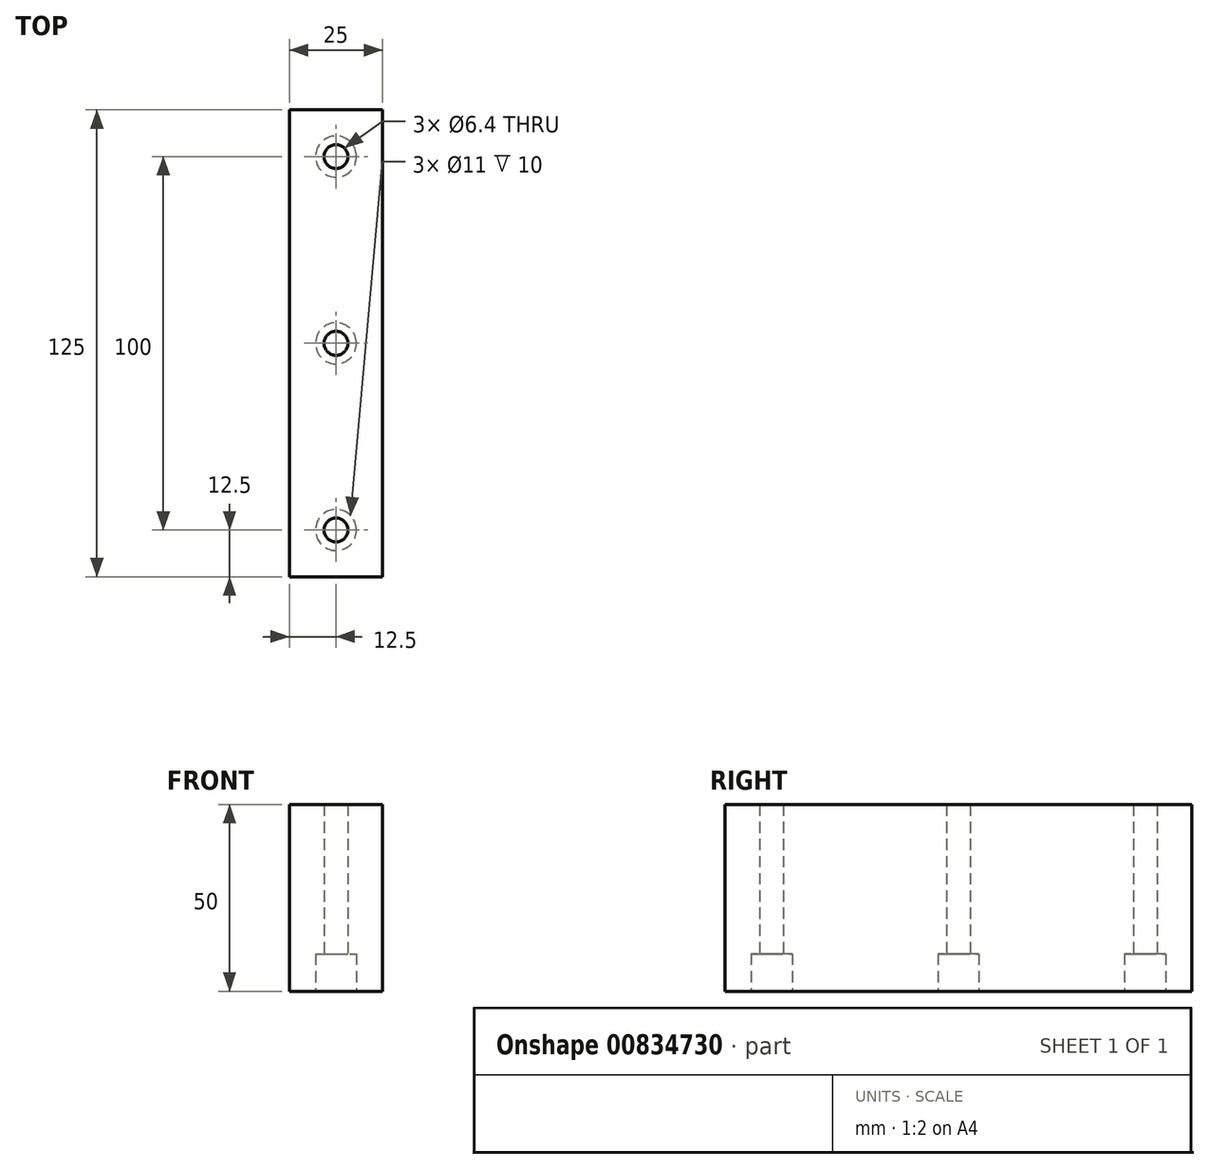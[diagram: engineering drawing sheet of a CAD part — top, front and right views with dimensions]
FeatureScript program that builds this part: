
annotation { "Feature Type Name" : "Feature", "Feature Type Description" : "" }
export const myFeature = defineFeature(function(context is Context, id is Id, definition is map)
    precondition{}
    {
        {
            var Q0;
            Q0=qCreatedBy(makeId("Top.planeOp"),FACE);
            var sketch = newSketch(context, id + "F0", { "sketchPlane" : qUnion([Q0])});
            skLineSegment(sketch, "E0.bottom", {"start": v(-12.5, 62.5) * mm, "end": v(12.5, 62.5) * mm});
            skLineSegment(sketch, "E0.top", {"start": v(-12.5, -62.5) * mm, "end": v(12.5, -62.5) * mm});
            skLineSegment(sketch, "E0.left", {"start": v(-12.5, 62.5) * mm, "end": v(-12.5, -62.5) * mm});
            skLineSegment(sketch, "E0.right", {"start": v(12.5, 62.5) * mm, "end": v(12.5, -62.5) * mm});
            skPoint(sketch, "E0.middle", {"position": v(0, 0) * mm});
            skSolve(sketch);
        }
        {
            var Q0;
            Q0=makeQuery(id+"F0.imprint","IMPRINT",FACE,{"disambiguationData":[TD([[makeQuery(id+"F0.imprint","IMPRINT",EDGE,{"derivedFrom":sQuery(id+"F0.wireOp",EDGE,"E0.bottom")}),-1.0]])]});
            extrude(context, id + "F1", {"entities" : qUnion([Q0]), "depth" : 50 * mm, "offsetDistance" : 25 * mm});
        }
        {
            var Q0;
            Q0=makeQuery(id+"F1.opExtrude","CAP_FACE",FACE,{"disambiguationData":[OSD([sQuery(id+"F0.wireOp",EDGE,"E0.bottom"),sQuery(id+"F0.wireOp",EDGE,"E0.top"),sQuery(id+"F0.wireOp",EDGE,"E0.left"),sQuery(id+"F0.wireOp",EDGE,"E0.right")])],"isStart":true});
            var sketch = newSketch(context, id + "F2", { "sketchPlane" : qUnion([Q0])});
            skLineSegment(sketch, "E1", {"start": v(0, 62.5) * mm, "end": v(0, -62.5) * mm});
            skPoint(sketch, "E2", {"position": v(0, -50) * mm});
            skPoint(sketch, "E3", {"position": v(0, 50) * mm});
            skPoint(sketch, "E4", {"position": v(0, 0) * mm});
            skSolve(sketch);
        }
        {
            var Q0;
            Q0=sQuery(id+"F2.wireOp",VERTEX,"E3");
            var Q1;
            Q1=sQuery(id+"F2.wireOp",VERTEX,"E2");
            var Q2;
            Q2=sQuery(id+"F2.wireOp",VERTEX,"E4");
            var Q3;
            Q3=makeQuery(id+"F1.opExtrude","SWEPT_BODY",BODY,{"disambiguationData":[OSD([sQuery(id+"F0.wireOp",EDGE,"E0.bottom"),sQuery(id+"F0.wireOp",EDGE,"E0.top"),sQuery(id+"F0.wireOp",EDGE,"E0.left"),sQuery(id+"F0.wireOp",EDGE,"E0.right")])]});
            hole(context, id + "F3", {"style" : HoleStyle.C_BORE, "endStyle" : HoleEndStyle.THROUGH, "holeDiameter" : 6.4 * mm, "cBoreDiameter" : 11 * mm, "cBoreDepth" : 10 * mm, "majorDiameter" : 5 * mm, "isTappedThrough" : true, "tappedDepth" : 12 * mm, "tapClearance" : 3, "locations" : qUnion([Q0, Q1, Q2]), "scope" : qUnion([Q3])});
        }
    });
